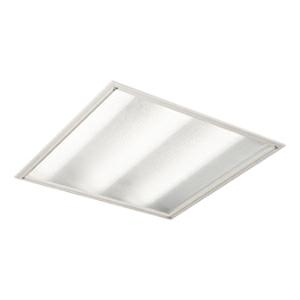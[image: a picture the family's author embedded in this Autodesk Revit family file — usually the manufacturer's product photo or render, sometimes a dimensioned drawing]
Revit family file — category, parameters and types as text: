
# Revit family: 3f_filippi_-_l_350_sp_3f_filippi_-_260092_-_l_353x14w_led_sp_54v_596x596
name_source: partatom
category: Lighting Fixtures
units: mm (PartAtom-declared; Revit-internal decimal feet)

## family parameters
Cut with Voids When Loaded = No
Host = Face
Light Source = No
Part Type = Normal
Room Calculation Point = No
Round Connector Dimension = Use Diameter
Shared = No

## types (1)
- 3F Filippi - L 350 SP (1 x LED, 6297 lm, 47 W, 4000 K)
    Apparent Load = 47 VA
    Approval mark = ENEC
    CIE Flux Codes = 59 88 97 100 100
    Color Rendering = 80
    Color Temperature = 4000 K
    Control Gear = Electronic ballast
    Default Elevation = 1800 mm
    Description = ILLUMINOTECHNICAL
Luminous efficiency 100% (DLOR 100%, ULOR 0%).
Initial luminous flux of the luminaire 6297 lm.
Direct symmetric distribution.
Installation Interdistance Transv.D = 1.27 x hu - Long.D = 1.21 x hu.
Tabular UGR (CIE 117 - 4H-8H; S=0.25H; 70/50/20): RUG 20.3 - 20.1.
Beam angle: 96° - 95°.
Luminous efficacy 134 lm/W.
Lifetime (L90/B10): 30000 h. (tq+25°C)
Lifetime (L85/B10): 50000 h. (tq+25°C)
Lifetime (L80/B20): 80000 h. (tq+25°C)
Lifetime (L70/B20): 100000 h. (tq+25°C)
Sudden decreased luminous flux after 50000 hours: 0% (C0).
Photobiological safety in compliance with IEC/TR 62778: RG0 risk exempt, (IEC 62471).
In compliance with IEC/EN 62722-2-1 - IEC/EN 62717 standards.

SOURCE
3 linear LED modules 14W/840.
Energy efficiency class (UE 2019/2020 - UE 2019/2015): C.
CIE 13.3 Colour rendering index: CRI >80 (R9 <50%).
IES TM-30 Fidelity Index: Rf = 84 Rg = 95.
CCT nominal colour temperature 4000 K.
Colour initial tolerance (MacAdam): SDCM 3.
Zhaga Book 7 compliant.

MECHANICAL
Housing in hot-galvanised steel, painted in white polyester.
Transparent methacrylate (PMMA) flat diffuser, multilenticular, anti-glare, with white painted aluminium frame, hinged opening.
Luminaire with limited surface temperature. - D - (EN 60598-2-24)
Dimensions: 596x596 mm, height 80 mm. Weight 4.525 kg.
IP54 protection degree for exposed part, IP20 for recessed part.
Mechanical strength to impacts IK06 (1 joule).
Glow-wire test resistance 650°C.

ELECTRICAL
Halogen Free electronic wiring 230V-50/60Hz, power factor 0.90, THD <25%, constant output current, class I, 1 driver.
Power of the luminaire 47 W.
CE - IEC 60598-1 - EN 60598-1.
SAFE FLICKER: PstLM=<1 and SVM=<0.4 (IEC TR 61547-1 and IEC TR 63158), to ensure a more comfortable and safe light.
Luminaire compliant with EN 60598-2-22 for power supply from a centralised emergency system CPSS (Central Power Supply System), not incorporated in the luminaire - high risk areas excluded. The default power and flux are 100% in AC and 100% in DC.
Ambient temperature from 0°C to +25°C.
Temperature class T6 max 85°C.
Quick connection.
Relative humidity UR: <85%.

INSTALLATION
Lay-in recessed fitting.
All accessories dedicated to this product are available on the Catalog and on our website www.3F-Filippi.com.

APPLICATIONS
In environments requiring protection, lamp shielding and simplified cleaning.

WARNING
Luminaire designed for disposal/recycling at end-of-life.
Replaceable (LED only) light source by a professional. Replaceable control gear by a professional.
    Height = 0 mm  [stored 0 ft]
    Lamp = 1 x LED
    Lamp Light Flux = 6297 lm
    Lamp Power = 47 W
    Lamp count = 1
    Length = 596 mm
    Lifetime = 50000 h
    Luminous efficacy = 134 lm/W
    Manufacturer = 3F Filippi
    ModVariant = No
    Model = 3F Filippi - 260092 - L 353x14W LED SP 54V 596x596
    Mounting Place = Ceiling
    Mounting Type = Recessed
    Number of Poles = 1
    OnlyDefault = Yes
    Power Factor = 1
    Product Name = 3F Filippi - L 350 SP
    Product group = recessed luminaire
    ProductGroupID = 4
    Protection Class = Protection class I
    Protection Degree = IP 20
    RLX_Detail_Level = 1
    RLX_Emergency_Light_Flux = 0 lm
    RLX_Emergency_Type = 0
    RLX_Emergency_Type_DB = No
    RlxData = <blob elided: 33457 chars, md5=884506ea>
    Socket = socket
    Standby Power = 0 W
    System Light Flux = 6297 lm
    System Power = 47 W
    Type Comments = Product without accessories
    Type Image = 3ffilippi_260092.jpg
    URL = http://relux.com
    VarID = ---
    Voltage = 0 V
    Weight = 0.00 kg
    Width = 596 mm

note: [stored X ft] marks values corroborated as IEEE doubles in the binary element streams (Revit-internal decimal feet)

## geometry (parser evidence)
native form markers: Blend x4, Sweep x10
no freeform markers — native parametric forms only
